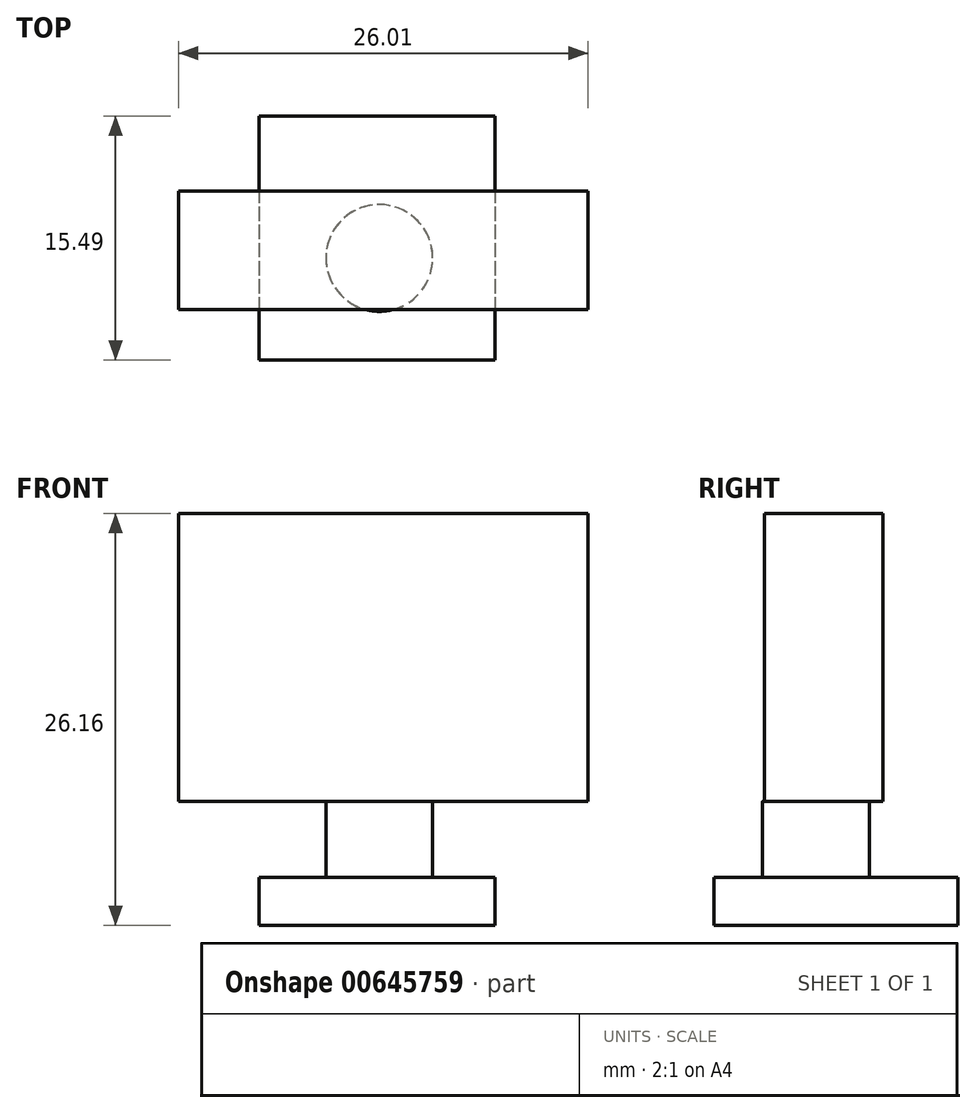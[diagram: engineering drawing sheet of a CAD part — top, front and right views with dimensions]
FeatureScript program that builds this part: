
annotation { "Feature Type Name" : "Feature", "Feature Type Description" : "" }
export const myFeature = defineFeature(function(context is Context, id is Id, definition is map)
    precondition{}
    {
        {
            var Q0;
            Q0=qCreatedBy(makeId("Top.planeOp"),FACE);
            var sketch = newSketch(context, id + "F0", { "sketchPlane" : qUnion([Q0])});
            skLineSegment(sketch, "E0.bottom", {"start": v(-7.63, 9.01) * mm, "end": v(7.35, 9.01) * mm});
            skLineSegment(sketch, "E0.top", {"start": v(-7.63, -6.48) * mm, "end": v(7.35, -6.48) * mm});
            skLineSegment(sketch, "E0.left", {"start": v(-7.63, 9.01) * mm, "end": v(-7.63, -6.48) * mm});
            skLineSegment(sketch, "E0.right", {"start": v(7.35, 9.01) * mm, "end": v(7.35, -6.48) * mm});
            skSolve(sketch);
        }
        {
            var Q0;
            Q0=makeQuery(id+"F0.imprint","IMPRINT",FACE,{"disambiguationData":[TD([[makeQuery(id+"F0.imprint","IMPRINT",EDGE,{"derivedFrom":sQuery(id+"F0.wireOp",EDGE,"E0.bottom")}),-1.0]])]});
            extrude(context, id + "F1", {"entities" : qUnion([Q0]), "depth" : 3.05 * mm, "offsetDistance" : 25.4 * mm});
        }
        {
            var Q0;
            Q0=qCreatedBy(makeId("Top.planeOp"),FACE);
            var sketch = newSketch(context, id + "F2", { "sketchPlane" : qUnion([Q0])});
            skCircle(sketch, "E1", {"center": v(0, 0) * mm, "radius": 3.4 * mm});
            skSolve(sketch);
        }
        {
            var Q0;
            Q0 = qSketchRegion(id + "F2", true);
            extrude(context, id + "F3", {"entities" : qUnion([Q0]), "operationType" : NewBodyOperationType.ADD, "depth" : 7.87 * mm, "offsetDistance" : 25.4 * mm});
        }
        {
            var Q0;
            Q0=makeQuery(id+"F3.opExtrude","CAP_FACE",FACE,{"disambiguationData":[OSD([sQuery(id+"F2.wireOp",EDGE,"E1")])],"isStart":false});
            var sketch = newSketch(context, id + "F4", { "sketchPlane" : qUnion([Q0])});
            skLineSegment(sketch, "E2.bottom", {"start": v(-12.76, 4.25) * mm, "end": v(13.25, 4.25) * mm});
            skLineSegment(sketch, "E2.top", {"start": v(-12.76, -3.28) * mm, "end": v(13.25, -3.28) * mm});
            skLineSegment(sketch, "E2.left", {"start": v(-12.76, 4.25) * mm, "end": v(-12.76, -3.28) * mm});
            skLineSegment(sketch, "E2.right", {"start": v(13.25, 4.25) * mm, "end": v(13.25, -3.28) * mm});
            skSolve(sketch);
        }
        {
            var Q0;
            Q0 = qSketchRegion(id + "F4", true);
            extrude(context, id + "F5", {"entities" : qUnion([Q0]), "operationType" : NewBodyOperationType.ADD, "depth" : 18.29 * mm, "offsetDistance" : 25.4 * mm});
        }
    });
